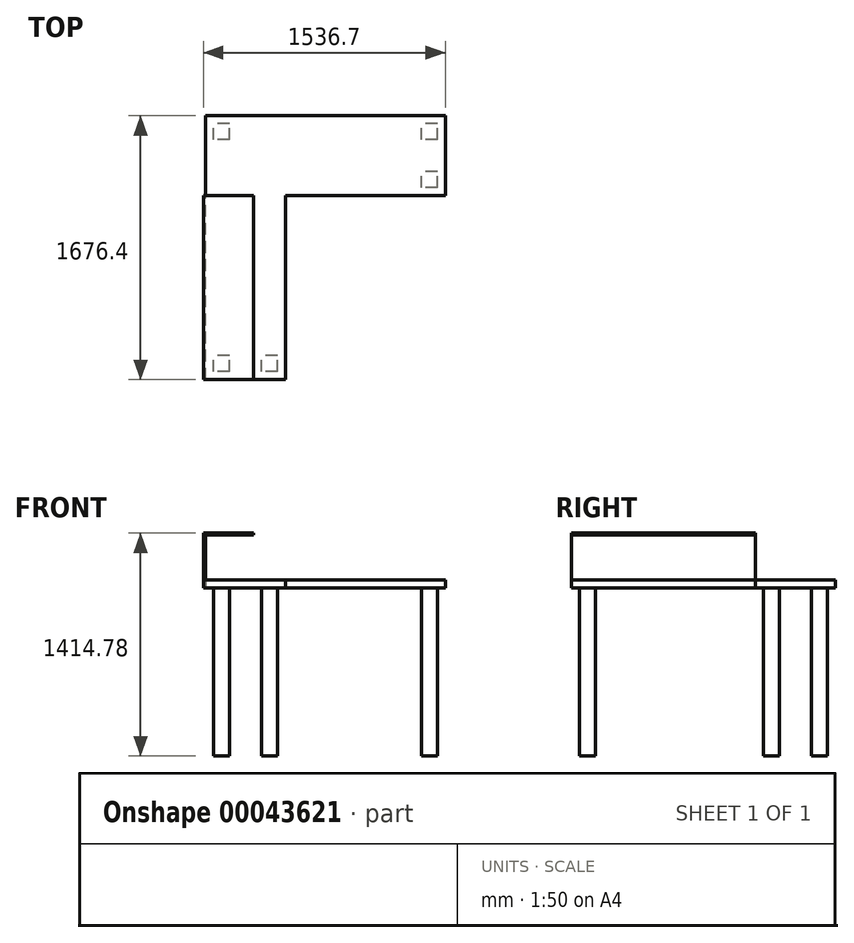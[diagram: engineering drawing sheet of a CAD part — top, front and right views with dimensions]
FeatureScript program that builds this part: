
annotation { "Feature Type Name" : "Feature", "Feature Type Description" : "" }
export const myFeature = defineFeature(function(context is Context, id is Id, definition is map)
    precondition{}
    {
        {
            var Q0;
            Q0=qCreatedBy(makeId("Top.planeOp"),FACE);
            var sketch = newSketch(context, id + "F0", { "sketchPlane" : qUnion([Q0])});
            skLineSegment(sketch, "E0.bottom", {"start": v(-508, -1168.4) * mm, "end": v(0, -1168.4) * mm});
            skLineSegment(sketch, "E0.top", {"start": v(-508, 508) * mm, "end": v(0, 508) * mm});
            skLineSegment(sketch, "E0.left", {"start": v(-508, -1168.4) * mm, "end": v(-508, 508) * mm});
            skLineSegment(sketch, "E0.right", {"start": v(0, -1168.4) * mm, "end": v(0, 508) * mm});
            skLineSegment(sketch, "E1.bottom", {"start": v(0, 508) * mm, "end": v(1016, 508) * mm});
            skLineSegment(sketch, "E1.top", {"start": v(0, 0) * mm, "end": v(1016, 0) * mm});
            skLineSegment(sketch, "E1.left", {"start": v(0, 508) * mm, "end": v(0, 0) * mm});
            skLineSegment(sketch, "E1.right", {"start": v(1016, 508) * mm, "end": v(1016, 0) * mm});
            skSolve(sketch);
        }
        {
            var Q0;
            Q0 = qSketchRegion(id + "F0", true);
            extrude(context, id + "F1", {"entities" : qUnion([Q0]), "oppositeDirection" : true, "depth" : 50.8 * mm});
        }
        {
            var Q0;
            Q0=makeQuery(id+"F1.opExtrude","CAP_FACE",FACE,{"disambiguationData":[OSD([sQuery(id+"F0.wireOp",EDGE,"E0.bottom"),sQuery(id+"F0.wireOp",EDGE,"E0.top"),sQuery(id+"F0.wireOp",EDGE,"E0.left"),sQuery(id+"F0.wireOp",EDGE,"E0.right"),sQuery(id+"F0.wireOp",EDGE,"E1.bottom"),sQuery(id+"F0.wireOp",EDGE,"E1.top"),sQuery(id+"F0.wireOp",EDGE,"E1.right")])],"isStart":false});
            var sketch = newSketch(context, id + "F2", { "sketchPlane" : qUnion([Q0])});
            skLineSegment(sketch, "E2.bottom", {"start": v(-50.8, 1117.6) * mm, "end": v(-152.4, 1117.6) * mm});
            skLineSegment(sketch, "E2.top", {"start": v(-50.8, 1016) * mm, "end": v(-152.4, 1016) * mm});
            skLineSegment(sketch, "E2.left", {"start": v(-50.8, 1117.6) * mm, "end": v(-50.8, 1016) * mm});
            skLineSegment(sketch, "E2.right", {"start": v(-152.4, 1117.6) * mm, "end": v(-152.4, 1016) * mm});
            skLineSegment(sketch, "E3.bottom", {"start": v(-355.6, 1117.6) * mm, "end": v(-457.2, 1117.6) * mm});
            skLineSegment(sketch, "E3.top", {"start": v(-355.6, 1016) * mm, "end": v(-457.2, 1016) * mm});
            skLineSegment(sketch, "E3.left", {"start": v(-355.6, 1117.6) * mm, "end": v(-355.6, 1016) * mm});
            skLineSegment(sketch, "E3.right", {"start": v(-457.2, 1117.6) * mm, "end": v(-457.2, 1016) * mm});
            skLineSegment(sketch, "E4.bottom", {"start": v(-355.6, -355.6) * mm, "end": v(-457.2, -355.6) * mm});
            skLineSegment(sketch, "E4.top", {"start": v(-355.6, -457.2) * mm, "end": v(-457.2, -457.2) * mm});
            skLineSegment(sketch, "E4.left", {"start": v(-355.6, -355.6) * mm, "end": v(-355.6, -457.2) * mm});
            skLineSegment(sketch, "E4.right", {"start": v(-457.2, -355.6) * mm, "end": v(-457.2, -457.2) * mm});
            skLineSegment(sketch, "E5.bottom", {"start": v(965.2, -50.8) * mm, "end": v(863.6, -50.8) * mm});
            skLineSegment(sketch, "E5.top", {"start": v(965.2, -152.4) * mm, "end": v(863.6, -152.4) * mm});
            skLineSegment(sketch, "E5.left", {"start": v(965.2, -50.8) * mm, "end": v(965.2, -152.4) * mm});
            skLineSegment(sketch, "E5.right", {"start": v(863.6, -50.8) * mm, "end": v(863.6, -152.4) * mm});
            skLineSegment(sketch, "E6.bottom", {"start": v(965.2, -355.6) * mm, "end": v(863.6, -355.6) * mm});
            skLineSegment(sketch, "E6.top", {"start": v(965.2, -457.2) * mm, "end": v(863.6, -457.2) * mm});
            skLineSegment(sketch, "E6.left", {"start": v(965.2, -355.6) * mm, "end": v(965.2, -457.2) * mm});
            skLineSegment(sketch, "E6.right", {"start": v(863.6, -355.6) * mm, "end": v(863.6, -457.2) * mm});
            skSolve(sketch);
        }
        {
            var Q0;
            Q0 = qSketchRegion(id + "F2", true);
            extrude(context, id + "F3", {"entities" : qUnion([Q0]), "operationType" : NewBodyOperationType.ADD, "depth" : 1066.8 * mm});
        }
        {
            var Q0;
            Q0=makeQuery(id+"F1.opExtrude","SWEPT_FACE",FACE,{"disambiguationData":[OSD([sQuery(id+"F0.wireOp",EDGE,"E0.left")])]});
            var sketch = newSketch(context, id + "F4", { "sketchPlane" : qUnion([Q0])});
            skLineSegment(sketch, "E7.bottom", {"start": v(0, 297.18) * mm, "end": v(1168.4, 297.18) * mm});
            skLineSegment(sketch, "E7.top", {"start": v(0, -50.8) * mm, "end": v(1168.4, -50.8) * mm});
            skLineSegment(sketch, "E7.left", {"start": v(0, 297.18) * mm, "end": v(0, -50.8) * mm});
            skLineSegment(sketch, "E7.right", {"start": v(1168.4, 297.18) * mm, "end": v(1168.4, -50.8) * mm});
            skSolve(sketch);
        }
        {
            var Q0;
            {var subQ0=sQuery(id+"F4.wireOp",EDGE,"E7.bottom");Q0=makeQuery(id+"F4.imprint","IMPRINT",FACE,{"disambiguationData":[TD([[makeQuery(id+"F4.imprint","IMPRINT",EDGE,{"derivedFrom":subQ0}),-1.0]])]});}
            var Q1;
            {var subQ0=sQuery(id+"F4.wireOp",EDGE,"E7.top");Q1=makeQuery(id+"F4.imprint","IMPRINT",FACE,{"disambiguationData":[TD([[makeQuery(id+"F4.imprint","IMPRINT",EDGE,{"derivedFrom":subQ0}),-1.0]])]});}
            extrude(context, id + "F5", {"entities" : qUnion([Q0, Q1]), "operationType" : NewBodyOperationType.ADD, "depth" : 12.7 * mm});
        }
        {
            var Q0;
            Q0=makeQuery(id+"F5.opExtrude","CAP_FACE",FACE,{"disambiguationData":[OSD([sQuery(id+"F4.wireOp",EDGE,"E7.bottom"),sQuery(id+"F4.wireOp",EDGE,"E7.top"),sQuery(id+"F4.wireOp",EDGE,"E7.left"),sQuery(id+"F4.wireOp",EDGE,"E7.right")])],"isStart":true});
            var sketch = newSketch(context, id + "F6", { "sketchPlane" : qUnion([Q0])});
            skLineSegment(sketch, "E8.bottom", {"start": v(-1168.4, 297.18) * mm, "end": v(508, 297.18) * mm});
            skLineSegment(sketch, "E8.top", {"start": v(-1168.4, 284.48) * mm, "end": v(508, 284.48) * mm});
            skLineSegment(sketch, "E8.left", {"start": v(-1168.4, 297.18) * mm, "end": v(-1168.4, 284.48) * mm});
            skLineSegment(sketch, "E8.right", {"start": v(508, 297.18) * mm, "end": v(508, 284.48) * mm});
            skSolve(sketch);
        }
        {
            var Q0;
            Q0=makeQuery(id+"F6.imprint","IMPRINT",FACE,{"disambiguationData":[TD([[makeQuery(id+"F6.imprint","IMPRINT",EDGE,{"derivedFrom":sQuery(id+"F6.wireOp",EDGE,"E8.bottom")}),1.0]])]});
            extrude(context, id + "F7", {"entities" : qUnion([Q0]), "operationType" : NewBodyOperationType.ADD, "depth" : 304.8 * mm});
        }
    });
